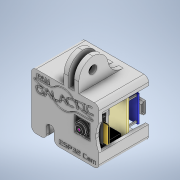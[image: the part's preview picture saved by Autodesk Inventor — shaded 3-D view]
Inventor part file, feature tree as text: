
AUTODESK INVENTOR PART (.ipt)
format: ipt  version: 2022 (Build 260153000, 153)  size: 1,457,152 bytes
history: native  units: in
note: dims shown in document units (in); Inventor stores cm internally (conversion verified against a paired STEP export)
features: extrude x31, sketch x30, fillet x4, chamfer x2, other x1
ambient origin geometry x8: Origin, YZ Plane, XZ Plane, XY Plane, X Axis, Y Axis, Z Axis, Center Point
bodies: Solid1 (feature_tree), Solid2 (feature_tree), Solid3 (feature_tree), Solid4 (feature_tree), Solid5 (feature_tree), Solid6 (feature_tree), Solid7 (feature_tree), Solid8 (feature_tree), Solid9 (feature_tree), Solid10 (feature_tree), Solid11 (feature_tree), Solid12 (feature_tree), Solid13 (feature_tree), Solid14 (feature_tree)
feature tree (68):
  extrude  "Extrusion1"  Depth=1.065in
  extrude  "Extrusion2"  Depth=0.7795in
  extrude  "Extrusion3"  Depth=0.0787in TaperAngle=0.0deg
  extrude  "Extrusion4"  Depth=0.2307in
  extrude  "Extrusion5"  Depth=0.0787in TaperAngle=0.0deg
  extrude  "Extrusion6"  Depth=0.1339in
  chamfer  "Chamfer1"  Distance=0.1476in
  extrude  "Extrusion7"  Depth=0.315in
  fillet  "Fillet2"  Radius=0.1575in
  extrude  "Extrusion8"  Depth=0.3217in
  extrude  "Extrusion9"  Depth=0.248in
  fillet  "Fillet3"  Radius=0.0512in
  extrude  "Extrusion10"  Depth=0.0394in TaperAngle=0.0deg
  extrude  "Extrusion11"  Depth=0.0787in
  extrude  "Extrusion12"  Depth=0.0315in
  fillet  "Fillet4"  Radius=0.0315in
  extrude  "Extrusion13"  Depth=0.0079in
  extrude  "Extrusion14"  Depth=0.4724in TaperAngle=0.0deg
  extrude  "Extrusion15"  Depth=0.0394in
  extrude  "Extrusion16"  Depth=0.0134in
  extrude  "Extrusion17"  Depth=0.5906in TaperAngle=0.0deg
  extrude  "Extrusion18"  Depth=0.0197in
  extrude  "Extrusion19"  Depth=0.7969in
  extrude  "Extrusion20"  Depth=0.0413in
  extrude  "Extrusion21"  Depth=0.6189in
  extrude  "Extrusion22"  Depth=0.0276in
  extrude  "Extrusion23"  Depth=0.1551in
  extrude  "Extrusion24"  Depth=0.0512in TaperAngle=0.0deg
  extrude  "Extrusion25"  Depth=0.0807in
  extrude  "Extrusion26"  Depth=0.0583in
  extrude  "Extrusion27"  Depth=0.0118in TaperAngle=0.0deg
  chamfer  "Chamfer2"  Distance=1.5472in
  extrude  "Extrusion28"  Depth=0.3937in
  extrude  "Extrusion29"  Depth=0.3937in
  fillet  "Fillet5"  Radius=0.1378in
  extrude  "Extrusion30"  Depth=0.3937in
  extrude  "Extrusion31"  Depth=0.3937in
  sketch  "Sketch1"  dims[d0=1.5591in d1=1.065in]
  sketch  "Sketch2"  dims[d2=0.5325in d3=0.7795in]
  sketch  "Sketch3"  dims[d4=0.0787in d5=0.063in d6=0.0in]
  sketch  "Sketch4"  dims[d7=0.5882in d8=0.2307in]
  sketch  "Sketch5"  dims[d9=0.2449in d10=0.0787in d11=0.0in]
  sketch  "Sketch6"  dims[d12=0.1339in d13=0.1339in]
  sketch  "Sketch7"  dims[d14=0.1811in]
  sketch  "Sketch8"  dims[d15=0.315in d16=0.1476in d17=0.0in]
  sketch  "Sketch9"  dims[d18=0.3098in d19=0.315in d20=0.1575in]
  sketch  "Sketch10"  dims[d21=0.1608in d22=0.3217in]
  sketch  "Sketch11"  dims[d23=0.0709in d24=0.0in d25=0.248in d26=0.0512in d27=0.0in]
  sketch  "Sketch12"  dims[d28=0.0669in d29=0.0394in d30=0.0in]
  sketch  "Sketch13"  dims[d31=0.0394in d32=0.0787in d33=45.0deg d35=0.0004in]
  sketch  "Sketch14"  dims[d36=0.0394in d37=0.0in d38=0.0315in d39=0.0315in]
  sketch  "Sketch15"  dims[d40=0.0079in d41=0.0972in]
  sketch  "Sketch16"  dims[d42=0.0472in d43=0.4724in d44=0.0in]
  sketch  "Sketch17"  dims[d45=0.4339in d46=0.0394in]
  sketch  "Sketch18"  dims[d47=0.0039in d48=0.0134in]
  sketch  "Sketch19"  dims[d49=0.0134in d50=0.5906in d51=0.0in]
  sketch  "Sketch20"  dims[d52=0.0197in d53=0.0937in]
  sketch  "Sketch21"  dims[d54=0.0937in d55=0.7969in]
  sketch  "Sketch22"  dims[d56=0.0394in d57=0.0413in]
  other  "Case Part A"
  sketch  "Sketch23"  dims[d58=0.1339in d59=0.6189in]
  sketch  "Sketch24"  dims[d60=0.4594in d61=0.0in d62=0.0276in]
  sketch  "Sketch26"  dims[d63=0.189in d64=0.1551in]
  sketch  "Sketch27"  dims[d65=0.2717in d66=0.0512in d67=0.0in]
  sketch  "Sketch28"  dims[d68=0.0693in d69=0.0807in]
  sketch  "Sketch29"  dims[d70=0.1614in d71=0.0583in]
  sketch  "Sketch30"  dims[d72=0.1165in d73=0.0118in d74=0.0in]
  sketch  "Sketch32"  dims[d75=0.0079in d76=1.5472in d77=1.2654in d78=0.1433in d79=0.1378in d80=0.0059in d81=0.0059in d82=0.0618in d83=0.0in d84=0.0394in d85=0.1465in d86=0.0039in d87=0.6693in d88=0.4362in d89=0.0in d90=0.2972in d91=0.2244in d94=0.4724in d95=0.0in d96=0.0335in d97=0.0335in d98=0.0335in d99=0.0335in d100=0.0335in d101=0.0335in d102=0.0335in d103=0.0157in d104=0.5472in d105=0.2697in d106=0.9016in d107=0.2252in d108=0.0in d109=0.6713in d110=0.0276in d111=0.3539in d112=1.0965in d113=0.4587in d114=0.0366in d115=0.0in d116=0.2961in d117=0.2142in d118=0.0512in d119=0.1876in d120=0.1876in d121=0.1098in d122=0.0in d125=0.2134in d126=0.0551in d127=0.0413in d128=0.0413in d129=0.0in d130=0.0in d131=0.0157in d132=0.0157in d133=0.0157in d134=0.0157in d135=0.0157in d136=0.0157in d137=0.0157in d138=0.0157in d139=0.2062in d140=0.0in d141=0.1181in d142=0.1181in d143=0.3406in d144=0.0358in d145=0.0335in d146=0.0in d147=0.065in d148=0.1969in d149=0.1969in d150=0.1969in d151=0.1969in d152=0.0197in d153=0.0197in d154=0.0197in d155=0.0197in d156=0.0197in d157=0.0197in d158=0.0197in d159=0.0197in d160=0.1772in d161=0.0in d162=0.0394in d163=0.0394in d164=0.0394in d166=0.0394in d168=0.0in d169=0.0787in d171=0.0787in d172=0.0394in d173=0.0394in d174=0.0394in d175=0.0787in d176=0.0394in d177=0.0394in d178=0.0394in d179=0.0394in d180=0.3799in d181=0.374in d182=0.3937in d183=0.7087in d184=0.0787in d185=0.0787in d186=0.1181in d187=0.1181in d188=0.0787in d189=0.0787in d190=0.0in d191=0.0079in d192=0.0079in d193=0.0079in d194=0.0079in d195=0.0in d198=0.0in d199=0.0in d201=0.0in d202=0.0in d203=0.0787in d204=0.0in d205=0.1181in d206=0.0079in d207=0.0079in d208=0.0768in d211=0.1181in d212=0.0079in d213=0.1181in d214=0.0709in d215=0.1082in d216=0.0079in d217=0.1181in d218=0.1082in d219=0.0709in d220=0.4564in d221=0.3701in d222=1.1811in d223=0.0in d224=0.0079in d225=0.0197in d226=0.3543in d227=0.0787in d228=0.0in d229=0.0197in d230=0.0787in d231=0.0in d232=0.0787in d233=0.3543in d234=0.4724in d235=0.0394in d236=0.0in d237=0.3543in d238=0.0394in d239=45.0deg d240=0.748in d241=0.1181in d242=0.1181in d243=0.1417in d244=0.3937in d245=0.6535in d246=0.0in d247=0.2067in d248=0.2992in d249=0.748in d250=0.3543in d251=0.0in d252=0.0in d253=0.3937in d254=0.0394in d255=0.0in d256=0.0394in d257=0.0in]
